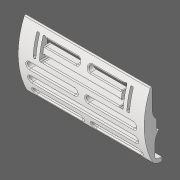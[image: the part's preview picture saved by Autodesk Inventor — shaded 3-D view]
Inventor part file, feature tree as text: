
AUTODESK INVENTOR PART (.ipt)
format: ipt  version: 2020 (Build 240168000, 168)  size: 697,856 bytes
history: native  units: in
note: dims shown in document units (in); Inventor stores cm internally (conversion verified against a paired STEP export)
features: extrude x3, fillet x2, other x2, sketch x2
ambient origin geometry x8: Origin, YZ Plane, XZ Plane, XY Plane, X Axis, Y Axis, Z Axis, Center Point
bodies: Solid1 (feature_tree)
feature tree (9):
  extrude  "Mounting Slots"  Depth=0.0591in
  extrude  "Strap Slots"  Depth=0.0118in
  fillet  "Fillet2"  Radius=0.0118in
  extrude  "Cosmetic Slots"  Depth=0.1181in
  fillet  "Fillet3"  Radius=0.2362in
  other  "Profile"
  other  "Slot Sketch"
  sketch  "Sketch3"  dims[d0=7.0866in d1=0.0in d3=0.0591in]
  sketch  "Sketch4"  dims[d5=0.5906in d14=0.0118in d15=0.0118in d16=0.1181in d17=0.2362in d18=0.1181in d19=0.3056in d20=0.2362in d21=0.5978in d22=0.0in d26=0.0118in d27=0.0118in d28=0.1181in d29=0.2362in d30=0.1181in d31=0.0079in d35=6.6142in d36=0.0118in d37=0.0118in d38=0.1181in d39=0.2362in d40=0.1181in d41=0.0079in d45=3.3071in d48=3.5433in d50=0.7874in d51=1.1811in d52=0.1575in d54=0.0in d55=0.0in d56=0.1969in d57=0.1969in d58=0.0591in d59=0.1575in d62=4.252in d71=0.0in d72=0.0in d83=3.5433in d85=0.2953in d86=0.6299in d87=0.3937in d88=0.3937in d89=0.3937in d92=0.6299in d93=0.0591in d95=0.3937in d96=0.6299in d97=0.3937in d98=4.252in d99=0.3937in d100=4.3307in d114=0.7874in d115=0.3056in d122=0.2362in d124=0.2362in d127=0.1181in d129=0.7874in d130=1.634in d131=0.4724in d133=0.7874in d134=0.2362in d135=0.1181in d136=0.3937in d137=4.7244in]
